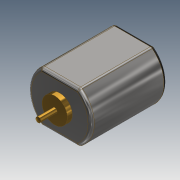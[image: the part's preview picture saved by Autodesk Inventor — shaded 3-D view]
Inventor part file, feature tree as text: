
AUTODESK INVENTOR PART (.ipt)
format: ipt  version: 2017 (Build 210142000, 142)  size: 146,944 bytes
history: native  units: mm
features: sketch x2, other x1, revolve x1, extrude x1, fillet x1
ambient origin geometry x8: Origin, YZ Plane, XZ Plane, XY Plane, X Axis, Y Axis, Z Axis, Center Point
bodies: Body1 (feature_tree)
feature tree (6):
  other  "Твердое тело1"
  revolve  "Вращение1"
  extrude  "Выдавливание1"  Depth=16.5mm
  fillet  "Сопряжение1"  Radius=0.8mm
  sketch  "Эскиз1"
  sketch  "Эскиз2"
